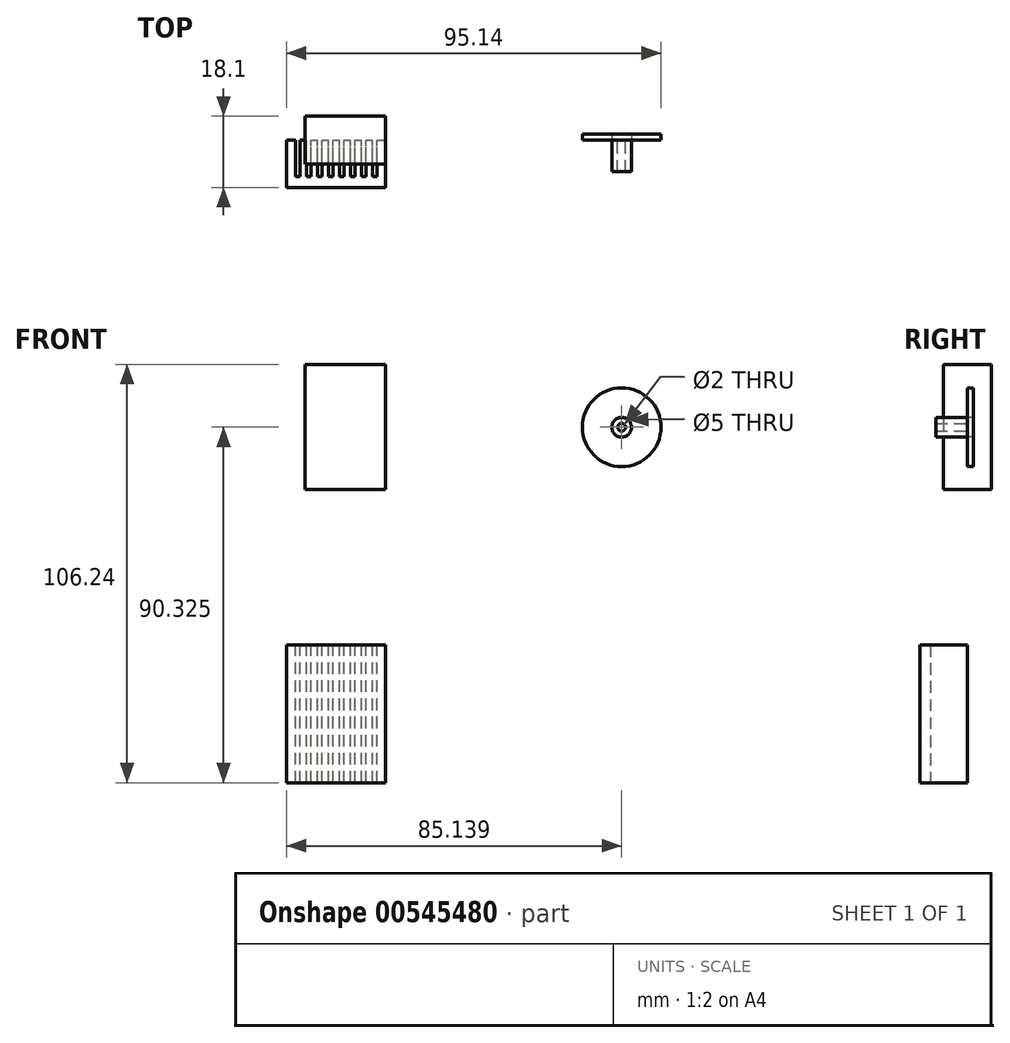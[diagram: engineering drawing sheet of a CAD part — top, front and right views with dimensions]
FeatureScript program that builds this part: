
annotation { "Feature Type Name" : "Feature", "Feature Type Description" : "" }
export const myFeature = defineFeature(function(context is Context, id is Id, definition is map)
    precondition{}
    {
        {
            var Q0;
            Q0=qCreatedBy(makeId("Front.planeOp"),FACE);
            var sketch = newSketch(context, id + "F0", { "sketchPlane" : qUnion([Q0])});
            skLineSegment(sketch, "E0.bottom", {"start": v(-49.52, 62.29) * mm, "end": v(-29.12, 62.29) * mm});
            skLineSegment(sketch, "E0.top", {"start": v(-49.52, 30.49) * mm, "end": v(-29.12, 30.49) * mm});
            skLineSegment(sketch, "E0.left", {"start": v(-49.52, 62.29) * mm, "end": v(-49.52, 30.49) * mm});
            skLineSegment(sketch, "E0.right", {"start": v(-29.12, 62.29) * mm, "end": v(-29.12, 30.49) * mm});
            skSolve(sketch);
        }
        {
            var Q0;
            Q0=qCreatedBy(makeId("Front.planeOp"),FACE);
            var sketch = newSketch(context, id + "F1", { "sketchPlane" : qUnion([Q0])});
            skLineSegment(sketch, "E1.bottom", {"start": v(-54.24, -8.95) * mm, "end": v(-29.14, -8.95) * mm});
            skLineSegment(sketch, "E1.top", {"start": v(-54.24, -43.95) * mm, "end": v(-29.14, -43.95) * mm});
            skLineSegment(sketch, "E1.left", {"start": v(-54.24, -8.95) * mm, "end": v(-54.24, -43.95) * mm});
            skLineSegment(sketch, "E1.right", {"start": v(-29.14, -8.95) * mm, "end": v(-29.14, -43.95) * mm});
            skSolve(sketch);
        }
        {
            var Q0;
            Q0=qCreatedBy(makeId("Front.planeOp"),FACE);
            var sketch = newSketch(context, id + "F2", { "sketchPlane" : qUnion([Q0])});
            skCircle(sketch, "E2", {"center": v(30.9, 46.38) * mm, "radius": 10 * mm});
            skCircle(sketch, "E3", {"center": v(30.9, 46.38) * mm, "radius": 2.5 * mm});
            skCircle(sketch, "E4.0", {"center": v(30.9, 46.38) * mm, "radius": 1 * mm});
            skSolve(sketch);
        }
        {
            var Q0;
            Q0 = qSketchRegion(id + "F0", true);
            var Q1;
            Q1 = qSketchRegion(id + "F5", true);
            extrude(context, id + "F3", {"entities" : qUnion([Q0, Q1]), "endBound" : BoundingType.SYMMETRIC, "depth" : 12.2 * mm, "offsetDistance" : 25 * mm});
        }
        {
            var Q0;
            Q0=makeQuery(id+"F1.imprint","IMPRINT",FACE,{"disambiguationData":[TD([[makeQuery(id+"F1.imprint","IMPRINT",EDGE,{"derivedFrom":sQuery(id+"F1.wireOp",EDGE,"E1.bottom")}),-1.0]])]});
            extrude(context, id + "F4", {"entities" : qUnion([Q0]), "depth" : 12 * mm, "offsetDistance" : 25 * mm});
        }
        {
            var Q0;
            Q0=makeQuery(id+"F4.opExtrude","CAP_FACE",FACE,{"disambiguationData":[OSD([sQuery(id+"F1.wireOp",EDGE,"E1.bottom"),sQuery(id+"F1.wireOp",EDGE,"E1.top"),sQuery(id+"F1.wireOp",EDGE,"E1.left"),sQuery(id+"F1.wireOp",EDGE,"E1.right")])],"isStart":true});
            var sketch = newSketch(context, id + "F5", { "sketchPlane" : qUnion([Q0])});
            skLineSegment(sketch, "E5.bottom", {"start": v(31.19, -8.95) * mm, "end": v(32.39, -8.95) * mm});
            skLineSegment(sketch, "E5.top", {"start": v(31.19, -43.95) * mm, "end": v(32.39, -43.95) * mm});
            skLineSegment(sketch, "E5.left", {"start": v(31.19, -8.95) * mm, "end": v(31.19, -43.95) * mm});
            skLineSegment(sketch, "E5.right", {"start": v(32.39, -8.95) * mm, "end": v(32.39, -43.95) * mm});
            skLineSegment(sketch, "E6.1.0.0", {"start": v(35.19, -8.94) * mm, "end": v(35.19, -43.94) * mm});
            skLineSegment(sketch, "E6.1.0.1", {"start": v(33.99, -8.94) * mm, "end": v(33.99, -43.94) * mm});
            skLineSegment(sketch, "E6.1.0.2", {"start": v(33.99, -43.94) * mm, "end": v(35.19, -43.94) * mm});
            skLineSegment(sketch, "E6.1.0.3", {"start": v(33.99, -8.94) * mm, "end": v(35.19, -8.94) * mm});
            skLineSegment(sketch, "E6.2.0.0", {"start": v(37.99, -8.93) * mm, "end": v(37.99, -43.93) * mm});
            skLineSegment(sketch, "E6.2.0.1", {"start": v(36.79, -8.93) * mm, "end": v(36.79, -43.93) * mm});
            skLineSegment(sketch, "E6.2.0.2", {"start": v(36.79, -43.93) * mm, "end": v(37.99, -43.93) * mm});
            skLineSegment(sketch, "E6.2.0.3", {"start": v(36.79, -8.93) * mm, "end": v(37.99, -8.93) * mm});
            skLineSegment(sketch, "E6.3.0.0", {"start": v(40.79, -8.93) * mm, "end": v(40.79, -43.93) * mm});
            skLineSegment(sketch, "E6.3.0.1", {"start": v(39.59, -8.93) * mm, "end": v(39.59, -43.93) * mm});
            skLineSegment(sketch, "E6.3.0.2", {"start": v(39.59, -43.93) * mm, "end": v(40.79, -43.93) * mm});
            skLineSegment(sketch, "E6.3.0.3", {"start": v(39.59, -8.93) * mm, "end": v(40.79, -8.93) * mm});
            skLineSegment(sketch, "E6.4.0.0", {"start": v(43.59, -8.92) * mm, "end": v(43.59, -43.92) * mm});
            skLineSegment(sketch, "E6.4.0.1", {"start": v(42.39, -8.92) * mm, "end": v(42.39, -43.92) * mm});
            skLineSegment(sketch, "E6.4.0.2", {"start": v(42.39, -43.92) * mm, "end": v(43.59, -43.92) * mm});
            skLineSegment(sketch, "E6.4.0.3", {"start": v(42.39, -8.92) * mm, "end": v(43.59, -8.92) * mm});
            skLineSegment(sketch, "E6.5.0.0", {"start": v(46.39, -8.92) * mm, "end": v(46.39, -43.92) * mm});
            skLineSegment(sketch, "E6.5.0.1", {"start": v(45.19, -8.92) * mm, "end": v(45.19, -43.92) * mm});
            skLineSegment(sketch, "E6.5.0.2", {"start": v(45.19, -43.92) * mm, "end": v(46.39, -43.92) * mm});
            skLineSegment(sketch, "E6.5.0.3", {"start": v(45.19, -8.92) * mm, "end": v(46.39, -8.92) * mm});
            skLineSegment(sketch, "E6.6.0.0", {"start": v(49.19, -8.9) * mm, "end": v(49.19, -43.9) * mm});
            skLineSegment(sketch, "E6.6.0.1", {"start": v(47.99, -8.9) * mm, "end": v(47.99, -43.9) * mm});
            skLineSegment(sketch, "E6.6.0.2", {"start": v(47.99, -43.9) * mm, "end": v(49.19, -43.9) * mm});
            skLineSegment(sketch, "E6.6.0.3", {"start": v(47.99, -8.9) * mm, "end": v(49.19, -8.9) * mm});
            skLineSegment(sketch, "E6.7.0.0", {"start": v(51.99, -8.9) * mm, "end": v(51.99, -43.9) * mm});
            skLineSegment(sketch, "E6.7.0.1", {"start": v(50.79, -8.9) * mm, "end": v(50.79, -43.9) * mm});
            skLineSegment(sketch, "E6.7.0.2", {"start": v(50.79, -43.9) * mm, "end": v(51.99, -43.9) * mm});
            skLineSegment(sketch, "E6.7.0.3", {"start": v(50.79, -8.9) * mm, "end": v(51.99, -8.9) * mm});
            skLineSegment(sketch, "E6.direction1", {"start": v(31.19, -43.95) * mm, "end": v(33.99, -43.94) * mm, "construction": true});
            skSolve(sketch);
        }
        {
            var Q0;
            Q0=makeQuery(id+"F5.imprint","IMPRINT",FACE,{"disambiguationData":[TD([[makeQuery(id+"F5.imprint","IMPRINT",EDGE,{"derivedFrom":sQuery(id+"F5.wireOp",EDGE,"E5.bottom")}),1.0]])]});
            var Q1;
            {var subQ0=sQuery(id+"F5.wireOp",EDGE,"E6.1.0.2");Q1=makeQuery(id+"F5.imprint","IMPRINT",FACE,{"disambiguationData":[TD([[makeQuery(id+"F5.imprint","IMPRINT",EDGE,{"derivedFrom":subQ0}),1.0]])]});}
            var Q2;
            {var subQ0=sQuery(id+"F5.wireOp",EDGE,"E6.2.0.2");Q2=makeQuery(id+"F5.imprint","IMPRINT",FACE,{"disambiguationData":[TD([[makeQuery(id+"F5.imprint","IMPRINT",EDGE,{"derivedFrom":subQ0}),1.0]])]});}
            var Q3;
            {var subQ0=sQuery(id+"F5.wireOp",EDGE,"E6.3.0.2");Q3=makeQuery(id+"F5.imprint","IMPRINT",FACE,{"disambiguationData":[TD([[makeQuery(id+"F5.imprint","IMPRINT",EDGE,{"derivedFrom":subQ0}),1.0]])]});}
            var Q4;
            {var subQ0=sQuery(id+"F5.wireOp",EDGE,"E6.4.0.2");Q4=makeQuery(id+"F5.imprint","IMPRINT",FACE,{"disambiguationData":[TD([[makeQuery(id+"F5.imprint","IMPRINT",EDGE,{"derivedFrom":subQ0}),1.0]])]});}
            var Q5;
            {var subQ0=sQuery(id+"F5.wireOp",EDGE,"E6.5.0.2");Q5=makeQuery(id+"F5.imprint","IMPRINT",FACE,{"disambiguationData":[TD([[makeQuery(id+"F5.imprint","IMPRINT",EDGE,{"derivedFrom":subQ0}),1.0]])]});}
            var Q6;
            {var subQ0=sQuery(id+"F5.wireOp",EDGE,"E6.6.0.2");Q6=makeQuery(id+"F5.imprint","IMPRINT",FACE,{"disambiguationData":[TD([[makeQuery(id+"F5.imprint","IMPRINT",EDGE,{"derivedFrom":subQ0}),1.0]])]});}
            var Q7;
            {var subQ0=sQuery(id+"F5.wireOp",EDGE,"E6.7.0.2");Q7=makeQuery(id+"F5.imprint","IMPRINT",FACE,{"disambiguationData":[TD([[makeQuery(id+"F5.imprint","IMPRINT",EDGE,{"derivedFrom":subQ0}),1.0]])]});}
            extrude(context, id + "F6", {"entities" : qUnion([Q0, Q1, Q2, Q3, Q4, Q5, Q6, Q7]), "operationType" : NewBodyOperationType.REMOVE, "endBound" : BoundingType.SYMMETRIC, "oppositeDirection" : true, "depth" : 10.6 * mm, "offsetDistance" : 25 * mm});
        }
        {
            var Q0;
            Q0=makeQuery(id+"F6.boolean.opBoolean","COPY",FACE,{"derivedFrom":makeQuery(id+"F6.opExtrude","SWEPT_FACE",FACE,{"disambiguationData":[OSD([sQuery(id+"F5.wireOp",EDGE,"E6.2.0.2")])]})});
            var Q1;
            Q1=makeQuery(id+"F6.boolean.opBoolean","COPY",FACE,{"derivedFrom":makeQuery(id+"F6.opExtrude","SWEPT_FACE",FACE,{"disambiguationData":[OSD([sQuery(id+"F5.wireOp",EDGE,"E6.3.0.2")])]})});
            var Q2;
            Q2=makeQuery(id+"F6.boolean.opBoolean","COPY",FACE,{"derivedFrom":makeQuery(id+"F6.opExtrude","SWEPT_FACE",FACE,{"disambiguationData":[OSD([sQuery(id+"F5.wireOp",EDGE,"E6.4.0.2")])]})});
            var Q3;
            Q3=makeQuery(id+"F6.boolean.opBoolean","COPY",FACE,{"derivedFrom":makeQuery(id+"F6.opExtrude","SWEPT_FACE",FACE,{"disambiguationData":[OSD([sQuery(id+"F5.wireOp",EDGE,"E6.5.0.2")])]})});
            var Q4;
            Q4=makeQuery(id+"F6.boolean.opBoolean","COPY",FACE,{"derivedFrom":makeQuery(id+"F6.opExtrude","SWEPT_FACE",FACE,{"disambiguationData":[OSD([sQuery(id+"F5.wireOp",EDGE,"E6.6.0.2")])]})});
            var Q5;
            Q5=makeQuery(id+"F6.boolean.opBoolean","COPY",FACE,{"derivedFrom":makeQuery(id+"F6.opExtrude","SWEPT_FACE",FACE,{"disambiguationData":[OSD([sQuery(id+"F5.wireOp",EDGE,"E6.7.0.2")])]})});
            extrude(context, id + "F7", {"entities" : qUnion([Q0, Q1, Q2, Q3, Q4, Q5]), "operationType" : NewBodyOperationType.REMOVE, "endBound" : BoundingType.SYMMETRIC, "oppositeDirection" : true, "depth" : 10.8 * mm, "offsetDistance" : 25 * mm});
        }
        {
            var Q0;
            {var subQ0=sQuery(id+"F5.wireOp",EDGE,"E6.7.0.2");Q0=makeQuery(id+"F7.boolean.opBoolean","MERGE",FACE,{"derivedFrom":[makeQuery(id+"F6.boolean.opBoolean","COPY",FACE,{"derivedFrom":makeQuery(id+"F6.opExtrude","CAP_FACE",FACE,{"disambiguationData":[OSD([sQuery(id+"F1.wireOp",EDGE,"E1.bottom"),sQuery(id+"F5.wireOp",EDGE,"E6.7.0.0"),sQuery(id+"F5.wireOp",EDGE,"E6.7.0.1"),subQ0])],"isStart":false})}),makeQuery(id+"F7.opExtrude","SWEPT_FACE",FACE,{"disambiguationData":[OSD([subQ0])]})]});}
            var Q1;
            {var subQ0=sQuery(id+"F5.wireOp",EDGE,"E6.6.0.2");Q1=makeQuery(id+"F7.boolean.opBoolean","MERGE",FACE,{"derivedFrom":[makeQuery(id+"F6.boolean.opBoolean","COPY",FACE,{"derivedFrom":makeQuery(id+"F6.opExtrude","CAP_FACE",FACE,{"disambiguationData":[OSD([sQuery(id+"F1.wireOp",EDGE,"E1.bottom"),sQuery(id+"F5.wireOp",EDGE,"E6.6.0.0"),sQuery(id+"F5.wireOp",EDGE,"E6.6.0.1"),subQ0])],"isStart":false})}),makeQuery(id+"F7.opExtrude","SWEPT_FACE",FACE,{"disambiguationData":[OSD([subQ0])]})]});}
            var Q2;
            {var subQ0=sQuery(id+"F5.wireOp",EDGE,"E6.5.0.2");Q2=makeQuery(id+"F7.boolean.opBoolean","MERGE",FACE,{"derivedFrom":[makeQuery(id+"F6.boolean.opBoolean","COPY",FACE,{"derivedFrom":makeQuery(id+"F6.opExtrude","CAP_FACE",FACE,{"disambiguationData":[OSD([sQuery(id+"F1.wireOp",EDGE,"E1.bottom"),sQuery(id+"F5.wireOp",EDGE,"E6.5.0.0"),sQuery(id+"F5.wireOp",EDGE,"E6.5.0.1"),subQ0])],"isStart":false})}),makeQuery(id+"F7.opExtrude","SWEPT_FACE",FACE,{"disambiguationData":[OSD([subQ0])]})]});}
            var Q3;
            {var subQ0=sQuery(id+"F5.wireOp",EDGE,"E6.4.0.2");Q3=makeQuery(id+"F7.boolean.opBoolean","MERGE",FACE,{"derivedFrom":[makeQuery(id+"F6.boolean.opBoolean","COPY",FACE,{"derivedFrom":makeQuery(id+"F6.opExtrude","CAP_FACE",FACE,{"disambiguationData":[OSD([sQuery(id+"F1.wireOp",EDGE,"E1.bottom"),sQuery(id+"F5.wireOp",EDGE,"E6.4.0.0"),sQuery(id+"F5.wireOp",EDGE,"E6.4.0.1"),subQ0])],"isStart":false})}),makeQuery(id+"F7.opExtrude","SWEPT_FACE",FACE,{"disambiguationData":[OSD([subQ0])]})]});}
            var Q4;
            {var subQ0=sQuery(id+"F5.wireOp",EDGE,"E6.3.0.2");Q4=makeQuery(id+"F7.boolean.opBoolean","MERGE",FACE,{"derivedFrom":[makeQuery(id+"F6.boolean.opBoolean","COPY",FACE,{"derivedFrom":makeQuery(id+"F6.opExtrude","CAP_FACE",FACE,{"disambiguationData":[OSD([sQuery(id+"F1.wireOp",EDGE,"E1.bottom"),sQuery(id+"F5.wireOp",EDGE,"E6.3.0.0"),sQuery(id+"F5.wireOp",EDGE,"E6.3.0.1"),subQ0])],"isStart":false})}),makeQuery(id+"F7.opExtrude","SWEPT_FACE",FACE,{"disambiguationData":[OSD([subQ0])]})]});}
            var Q5;
            {var subQ0=sQuery(id+"F5.wireOp",EDGE,"E6.2.0.2");Q5=makeQuery(id+"F7.boolean.opBoolean","MERGE",FACE,{"derivedFrom":[makeQuery(id+"F6.boolean.opBoolean","COPY",FACE,{"derivedFrom":makeQuery(id+"F6.opExtrude","CAP_FACE",FACE,{"disambiguationData":[OSD([sQuery(id+"F1.wireOp",EDGE,"E1.bottom"),sQuery(id+"F5.wireOp",EDGE,"E6.2.0.0"),sQuery(id+"F5.wireOp",EDGE,"E6.2.0.1"),subQ0])],"isStart":false})}),makeQuery(id+"F7.opExtrude","SWEPT_FACE",FACE,{"disambiguationData":[OSD([subQ0])]})]});}
            var Q6;
            Q6=makeQuery(id+"F6.boolean.opBoolean","COPY",FACE,{"derivedFrom":makeQuery(id+"F6.opExtrude","CAP_FACE",FACE,{"disambiguationData":[OSD([sQuery(id+"F1.wireOp",EDGE,"E1.bottom"),sQuery(id+"F5.wireOp",EDGE,"E6.1.0.0"),sQuery(id+"F5.wireOp",EDGE,"E6.1.0.1"),sQuery(id+"F5.wireOp",EDGE,"E6.1.0.2")])],"isStart":false})});
            var Q7;
            Q7=makeQuery(id+"F6.boolean.opBoolean","COPY",FACE,{"derivedFrom":makeQuery(id+"F6.opExtrude","CAP_FACE",FACE,{"disambiguationData":[OSD([sQuery(id+"F5.wireOp",EDGE,"E5.bottom"),sQuery(id+"F5.wireOp",EDGE,"E5.top"),sQuery(id+"F5.wireOp",EDGE,"E5.left"),sQuery(id+"F5.wireOp",EDGE,"E5.right")])],"isStart":false})});
            extrude(context, id + "F8", {"entities" : qUnion([Q0, Q1, Q2, Q3, Q4, Q5, Q6, Q7]), "operationType" : NewBodyOperationType.REMOVE, "endBound" : BoundingType.SYMMETRIC, "depth" : 8 * mm, "offsetDistance" : 25 * mm});
        }
        {
            var Q0;
            Q0=makeQuery(id+"F2.imprint","IMPRINT",FACE,{"disambiguationData":[TD([[makeQuery(id+"F2.imprint","IMPRINT",EDGE,{"derivedFrom":sQuery(id+"F2.wireOp",EDGE,"E3")}),1.0]])]});
            extrude(context, id + "F9", {"entities" : qUnion([Q0]), "depth" : 8 * mm, "offsetDistance" : 25 * mm});
        }
        {
            var Q0;
            Q0=makeQuery(id+"F2.imprint","IMPRINT",FACE,{"disambiguationData":[TD([[makeQuery(id+"F2.imprint","IMPRINT",EDGE,{"derivedFrom":sQuery(id+"F2.wireOp",EDGE,"E2")}),1.0]])]});
            extrude(context, id + "F10", {"entities" : qUnion([Q0]), "oppositeDirection" : true, "depth" : 1.5 * mm, "offsetDistance" : 25 * mm});
        }
    });
